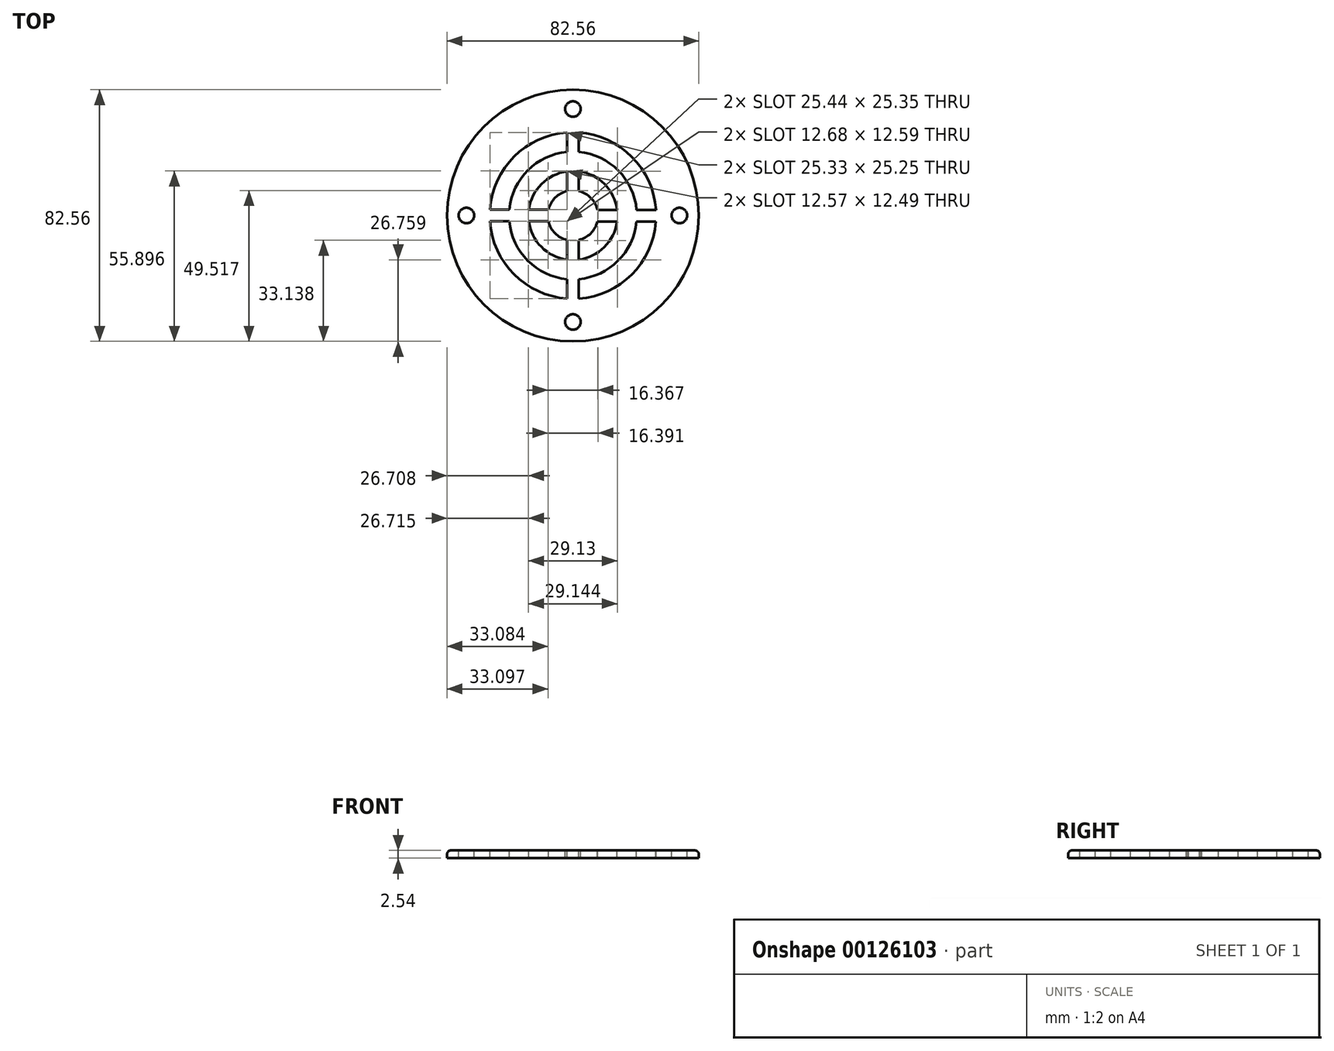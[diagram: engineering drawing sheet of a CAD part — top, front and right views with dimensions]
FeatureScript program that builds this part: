
annotation { "Feature Type Name" : "Feature", "Feature Type Description" : "" }
export const myFeature = defineFeature(function(context is Context, id is Id, definition is map)
    precondition{}
    {
        {
            var Q0;
            Q0=qCreatedBy(makeId("Top.planeOp"),FACE);
            var sketch = newSketch(context, id + "F0", { "sketchPlane" : qUnion([Q0])});
            skCircle(sketch, "E0", {"center": v(0, 0) * mm, "radius": 41.28 * mm});
            skSolve(sketch);
        }
        {
            var Q0;
            Q0 = qSketchRegion(id + "F0", true);
            extrude(context, id + "F1", {"entities" : qUnion([Q0]), "depth" : 2.54 * mm});
        }
        {
            var Q0;
            Q0=makeQuery(id+"F1.opExtrude","CAP_FACE",FACE,{"disambiguationData":[OSD([sQuery(id+"F0.wireOp",EDGE,"E0")])],"isStart":false});
            var sketch = newSketch(context, id + "F2", { "sketchPlane" : qUnion([Q0])});
            skCircle(sketch, "E1", {"center": v(0, 34.93) * mm, "radius": 2.54 * mm});
            skSolve(sketch);
        }
        {
            var Q0;
            Q0 = qSketchRegion(id + "F2", true);
            extrude(context, id + "F3", {"entities" : qUnion([Q0]), "operationType" : NewBodyOperationType.REMOVE, "endBound" : BoundingType.THROUGH_ALL, "oppositeDirection" : true, "depth" : 25.4 * mm});
        }
        {
            var Q0;
            Q0=makeQuery(id+"F1.opExtrude","CAP_FACE",FACE,{"disambiguationData":[OSD([sQuery(id+"F0.wireOp",EDGE,"E0")])],"isStart":false});
            var sketch = newSketch(context, id + "F4", { "sketchPlane" : qUnion([Q0])});
            skCircle(sketch, "E2", {"center": v(0, -34.93) * mm, "radius": 2.54 * mm});
            skSolve(sketch);
        }
        {
            var Q0;
            Q0 = qSketchRegion(id + "F4", true);
            extrude(context, id + "F5", {"entities" : qUnion([Q0]), "operationType" : NewBodyOperationType.REMOVE, "endBound" : BoundingType.THROUGH_ALL, "oppositeDirection" : true, "depth" : 25.4 * mm});
        }
        {
            var Q0;
            Q0=makeQuery(id+"F1.opExtrude","CAP_FACE",FACE,{"disambiguationData":[OSD([sQuery(id+"F0.wireOp",EDGE,"E0")])],"isStart":false});
            var sketch = newSketch(context, id + "F6", { "sketchPlane" : qUnion([Q0])});
            skCircle(sketch, "E3", {"center": v(-34.93, 0) * mm, "radius": 2.54 * mm});
            skSolve(sketch);
        }
        {
            var Q0;
            Q0 = qSketchRegion(id + "F6", true);
            extrude(context, id + "F7", {"entities" : qUnion([Q0]), "operationType" : NewBodyOperationType.REMOVE, "endBound" : BoundingType.THROUGH_ALL, "oppositeDirection" : true, "depth" : 25.4 * mm});
        }
        {
            var Q0;
            Q0=makeQuery(id+"F1.opExtrude","CAP_FACE",FACE,{"disambiguationData":[OSD([sQuery(id+"F0.wireOp",EDGE,"E0")])],"isStart":false});
            var sketch = newSketch(context, id + "F8", { "sketchPlane" : qUnion([Q0])});
            skCircle(sketch, "E4", {"center": v(34.93, 0) * mm, "radius": 2.54 * mm});
            skSolve(sketch);
        }
        {
            var Q0;
            Q0 = qSketchRegion(id + "F8", true);
            extrude(context, id + "F9", {"entities" : qUnion([Q0]), "operationType" : NewBodyOperationType.REMOVE, "endBound" : BoundingType.THROUGH_ALL, "oppositeDirection" : true, "depth" : 25.4 * mm});
        }
        {
            var Q0;
            Q0=makeQuery(id+"F1.opExtrude","CAP_EDGE",EDGE,{"disambiguationData":[OSD([sQuery(id+"F0.wireOp",EDGE,"E0")])],"isStart":false});
            fillet(context, id + "F10", {"entities" : qUnion([Q0]), "radius" : 1.27 * mm, "tangentPropagation" : true, "allowEdgeOverflow" : false});
        }
        {
            var Q0;
            Q0=makeQuery(id+"F1.opExtrude","CAP_FACE",FACE,{"disambiguationData":[OSD([sQuery(id+"F0.wireOp",EDGE,"E0")])],"isStart":false});
            var sketch = newSketch(context, id + "F11", { "sketchPlane" : qUnion([Q0])});
            skCircle(sketch, "E5", {"center": v(0, 0) * mm, "radius": 27.3 * mm});
            skSolve(sketch);
        }
        {
            var Q0;
            Q0 = qSketchRegion(id + "F11", true);
            extrude(context, id + "F12", {"entities" : qUnion([Q0]), "operationType" : NewBodyOperationType.REMOVE, "endBound" : BoundingType.THROUGH_ALL, "oppositeDirection" : true, "depth" : 25.4 * mm});
        }
        {
            var Q0;
            Q0=makeQuery(id+"F1.opExtrude","CAP_FACE",FACE,{"disambiguationData":[OSD([sQuery(id+"F0.wireOp",EDGE,"E0")])],"isStart":false});
            var sketch = newSketch(context, id + "F13", { "sketchPlane" : qUnion([Q0])});
            skCircle(sketch, "E6", {"center": v(0, 0) * mm, "radius": 20.96 * mm});
            skSolve(sketch);
        }
        {
            var Q0;
            Q0 = qSketchRegion(id + "F13", true);
            extrude(context, id + "F14", {"entities" : qUnion([Q0]), "oppositeDirection" : true, "depth" : 2.54 * mm});
        }
        {
            var Q0;
            Q0=makeQuery(id+"F14.opExtrude","CAP_FACE",FACE,{"disambiguationData":[OSD([sQuery(id+"F13.wireOp",EDGE,"E6")])],"isStart":true});
            var sketch = newSketch(context, id + "F15", { "sketchPlane" : qUnion([Q0])});
            skCircle(sketch, "E7", {"center": v(0, 0) * mm, "radius": 14.6 * mm});
            skSolve(sketch);
        }
        {
            var Q0;
            Q0 = qSketchRegion(id + "F15", true);
            extrude(context, id + "F16", {"entities" : qUnion([Q0]), "operationType" : NewBodyOperationType.REMOVE, "endBound" : BoundingType.THROUGH_ALL, "oppositeDirection" : true, "depth" : 25.4 * mm});
        }
        {
            var Q0;
            Q0=makeQuery(id+"F1.opExtrude","CAP_FACE",FACE,{"disambiguationData":[OSD([sQuery(id+"F0.wireOp",EDGE,"E0")])],"isStart":false});
            var sketch = newSketch(context, id + "F17", { "sketchPlane" : qUnion([Q0])});
            skCircle(sketch, "E8", {"center": v(0, 0) * mm, "radius": 8.26 * mm});
            skSolve(sketch);
        }
        {
            var Q0;
            Q0 = qSketchRegion(id + "F17", true);
            extrude(context, id + "F18", {"entities" : qUnion([Q0]), "oppositeDirection" : true, "depth" : 2.54 * mm});
        }
        {
            var Q0;
            Q0=makeQuery(id+"F1.opExtrude","CAP_FACE",FACE,{"disambiguationData":[OSD([sQuery(id+"F0.wireOp",EDGE,"E0")])],"isStart":false});
            var sketch = newSketch(context, id + "F19", { "sketchPlane" : qUnion([Q0])});
            skLineSegment(sketch, "E9.bottom", {"start": v(-1.9, -5.03) * mm, "end": v(1.9, -5.03) * mm});
            skLineSegment(sketch, "E9.top", {"start": v(-1.9, -29.9) * mm, "end": v(1.9, -29.9) * mm});
            skLineSegment(sketch, "E9.left", {"start": v(-1.9, -5.03) * mm, "end": v(-1.9, -29.9) * mm});
            skLineSegment(sketch, "E9.right", {"start": v(1.9, -5.03) * mm, "end": v(1.9, -29.9) * mm});
            skSolve(sketch);
        }
        {
            var Q0;
            Q0 = qSketchRegion(id + "F19", true);
            extrude(context, id + "F20", {"entities" : qUnion([Q0]), "operationType" : NewBodyOperationType.ADD, "oppositeDirection" : true, "depth" : 2.54 * mm});
        }
        {
            var Q0;
            Q0=makeQuery(id+"F20.boolean.opBoolean","MERGE",FACE,{"derivedFrom":[makeQuery(id+"F1.opExtrude","CAP_FACE",FACE,{"disambiguationData":[OSD([sQuery(id+"F0.wireOp",EDGE,"E0")])],"isStart":false}),makeQuery(id+"F14.opExtrude","CAP_FACE",FACE,{"disambiguationData":[OSD([sQuery(id+"F13.wireOp",EDGE,"E6")])],"isStart":true}),makeQuery(id+"F18.opExtrude","CAP_FACE",FACE,{"disambiguationData":[OSD([sQuery(id+"F17.wireOp",EDGE,"E8")])],"isStart":true}),makeQuery(id+"F20.opExtrude","CAP_FACE",FACE,{"disambiguationData":[OSD([sQuery(id+"F19.wireOp",EDGE,"E9.bottom"),sQuery(id+"F19.wireOp",EDGE,"E9.top"),sQuery(id+"F19.wireOp",EDGE,"E9.left"),sQuery(id+"F19.wireOp",EDGE,"E9.right")])],"isStart":true})]});
            var sketch = newSketch(context, id + "F21", { "sketchPlane" : qUnion([Q0])});
            skLineSegment(sketch, "E10.bottom", {"start": v(4.56, 1.8) * mm, "end": v(29.42, 1.8) * mm});
            skLineSegment(sketch, "E10.top", {"start": v(4.56, -2) * mm, "end": v(29.42, -2) * mm});
            skLineSegment(sketch, "E10.left", {"start": v(4.56, 1.8) * mm, "end": v(4.56, -2) * mm});
            skLineSegment(sketch, "E10.right", {"start": v(29.42, 1.8) * mm, "end": v(29.42, -2) * mm});
            skSolve(sketch);
        }
        {
            var Q0;
            Q0 = qSketchRegion(id + "F21", true);
            extrude(context, id + "F22", {"entities" : qUnion([Q0]), "operationType" : NewBodyOperationType.ADD, "oppositeDirection" : true, "depth" : 2.54 * mm});
        }
        {
            var Q0;
            Q0=makeQuery(id+"F22.boolean.opBoolean","MERGE",FACE,{"derivedFrom":[makeQuery(id+"F20.boolean.opBoolean","MERGE",FACE,{"derivedFrom":[makeQuery(id+"F1.opExtrude","CAP_FACE",FACE,{"disambiguationData":[OSD([sQuery(id+"F0.wireOp",EDGE,"E0")])],"isStart":false}),makeQuery(id+"F14.opExtrude","CAP_FACE",FACE,{"disambiguationData":[OSD([sQuery(id+"F13.wireOp",EDGE,"E6")])],"isStart":true}),makeQuery(id+"F18.opExtrude","CAP_FACE",FACE,{"disambiguationData":[OSD([sQuery(id+"F17.wireOp",EDGE,"E8")])],"isStart":true}),makeQuery(id+"F20.opExtrude","CAP_FACE",FACE,{"disambiguationData":[OSD([sQuery(id+"F19.wireOp",EDGE,"E9.bottom"),sQuery(id+"F19.wireOp",EDGE,"E9.top"),sQuery(id+"F19.wireOp",EDGE,"E9.left"),sQuery(id+"F19.wireOp",EDGE,"E9.right")])],"isStart":true})]}),makeQuery(id+"F22.opExtrude","CAP_FACE",FACE,{"disambiguationData":[OSD([sQuery(id+"F21.wireOp",EDGE,"E10.bottom"),sQuery(id+"F21.wireOp",EDGE,"E10.top"),sQuery(id+"F21.wireOp",EDGE,"E10.left"),sQuery(id+"F21.wireOp",EDGE,"E10.right")])],"isStart":true})]});
            var sketch = newSketch(context, id + "F23", { "sketchPlane" : qUnion([Q0])});
            skLineSegment(sketch, "E11.bottom", {"start": v(-1.9, 30.09) * mm, "end": v(1.9, 30.09) * mm});
            skLineSegment(sketch, "E11.top", {"start": v(-1.9, 4.27) * mm, "end": v(1.9, 4.27) * mm});
            skLineSegment(sketch, "E11.left", {"start": v(-1.9, 30.09) * mm, "end": v(-1.9, 4.27) * mm});
            skLineSegment(sketch, "E11.right", {"start": v(1.9, 30.09) * mm, "end": v(1.9, 4.27) * mm});
            skSolve(sketch);
        }
        {
            var Q0;
            Q0 = qSketchRegion(id + "F23", true);
            extrude(context, id + "F24", {"entities" : qUnion([Q0]), "operationType" : NewBodyOperationType.ADD, "oppositeDirection" : true, "depth" : 2.54 * mm});
        }
        {
            var Q0;
            Q0=makeQuery(id+"F24.boolean.opBoolean","MERGE",FACE,{"derivedFrom":[makeQuery(id+"F22.boolean.opBoolean","MERGE",FACE,{"derivedFrom":[makeQuery(id+"F20.boolean.opBoolean","MERGE",FACE,{"derivedFrom":[makeQuery(id+"F1.opExtrude","CAP_FACE",FACE,{"disambiguationData":[OSD([sQuery(id+"F0.wireOp",EDGE,"E0")])],"isStart":false}),makeQuery(id+"F14.opExtrude","CAP_FACE",FACE,{"disambiguationData":[OSD([sQuery(id+"F13.wireOp",EDGE,"E6")])],"isStart":true}),makeQuery(id+"F18.opExtrude","CAP_FACE",FACE,{"disambiguationData":[OSD([sQuery(id+"F17.wireOp",EDGE,"E8")])],"isStart":true}),makeQuery(id+"F20.opExtrude","CAP_FACE",FACE,{"disambiguationData":[OSD([sQuery(id+"F19.wireOp",EDGE,"E9.bottom"),sQuery(id+"F19.wireOp",EDGE,"E9.top"),sQuery(id+"F19.wireOp",EDGE,"E9.left"),sQuery(id+"F19.wireOp",EDGE,"E9.right")])],"isStart":true})]}),makeQuery(id+"F22.opExtrude","CAP_FACE",FACE,{"disambiguationData":[OSD([sQuery(id+"F21.wireOp",EDGE,"E10.bottom"),sQuery(id+"F21.wireOp",EDGE,"E10.top"),sQuery(id+"F21.wireOp",EDGE,"E10.left"),sQuery(id+"F21.wireOp",EDGE,"E10.right")])],"isStart":true})]}),makeQuery(id+"F24.opExtrude","CAP_FACE",FACE,{"disambiguationData":[OSD([sQuery(id+"F23.wireOp",EDGE,"E11.bottom"),sQuery(id+"F23.wireOp",EDGE,"E11.top"),sQuery(id+"F23.wireOp",EDGE,"E11.left"),sQuery(id+"F23.wireOp",EDGE,"E11.right")])],"isStart":true})]});
            var sketch = newSketch(context, id + "F25", { "sketchPlane" : qUnion([Q0])});
            skLineSegment(sketch, "E12.bottom", {"start": v(-30.56, 2) * mm, "end": v(-5.7, 2) * mm});
            skLineSegment(sketch, "E12.top", {"start": v(-30.56, -1.8) * mm, "end": v(-5.7, -1.8) * mm});
            skLineSegment(sketch, "E12.left", {"start": v(-30.56, 2) * mm, "end": v(-30.56, -1.8) * mm});
            skLineSegment(sketch, "E12.right", {"start": v(-5.7, 2) * mm, "end": v(-5.7, -1.8) * mm});
            skSolve(sketch);
        }
        {
            var Q0;
            Q0 = qSketchRegion(id + "F25", true);
            extrude(context, id + "F26", {"entities" : qUnion([Q0]), "operationType" : NewBodyOperationType.ADD, "oppositeDirection" : true, "depth" : 2.54 * mm});
        }
    });
